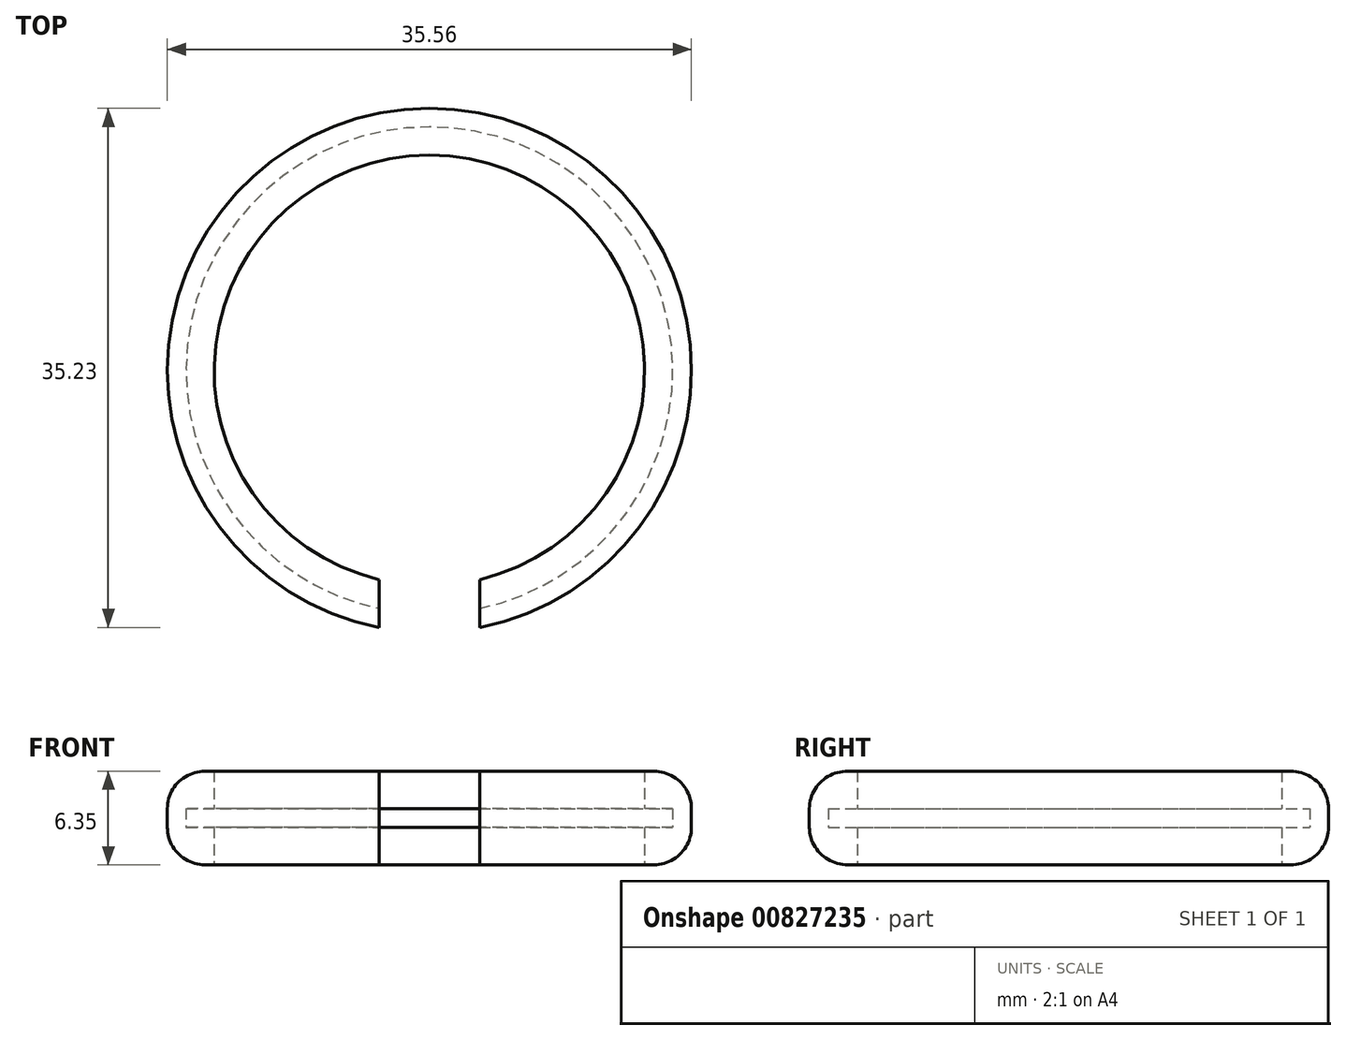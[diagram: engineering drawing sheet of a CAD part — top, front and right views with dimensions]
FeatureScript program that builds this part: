
annotation { "Feature Type Name" : "Feature", "Feature Type Description" : "" }
export const myFeature = defineFeature(function(context is Context, id is Id, definition is map)
    precondition{}
    {
        {
            var Q0;
            Q0=qCreatedBy(makeId("Top.planeOp"),FACE);
            var sketch = newSketch(context, id + "F0", { "sketchPlane" : qUnion([Q0])});
            skCircle(sketch, "E0", {"center": v(0, 0) * mm, "radius": 17.78 * mm});
            skSolve(sketch);
        }
        {
            var Q0;
            Q0=makeQuery(id+"F0.imprint","IMPRINT",FACE,{"disambiguationData":[TD([[makeQuery(id+"F0.imprint","IMPRINT",EDGE,{"derivedFrom":sQuery(id+"F0.wireOp",EDGE,"E0")}),1.0]])]});
            extrude(context, id + "F1", {"entities" : qUnion([Q0]), "depth" : 2.54 * mm, "offsetDistance" : 25.4 * mm});
        }
        {
            var Q0;
            Q0=makeQuery(id+"F1.opExtrude","CAP_FACE",FACE,{"disambiguationData":[OSD([sQuery(id+"F0.wireOp",EDGE,"E0")])],"isStart":false});
            var sketch = newSketch(context, id + "F2", { "sketchPlane" : qUnion([Q0])});
            skCircle(sketch, "E1", {"center": v(0, 0) * mm, "radius": 17.78 * mm});
            skCircle(sketch, "E2", {"center": v(0, 0) * mm, "radius": 16.51 * mm});
            skSolve(sketch);
        }
        {
            var Q0;
            Q0=makeQuery(id+"F2.imprint","IMPRINT",FACE,{"disambiguationData":[TD([[makeQuery(id+"F2.imprint","IMPRINT",EDGE,{"derivedFrom":sQuery(id+"F2.wireOp",EDGE,"E2")}),-1.0]])]});
            extrude(context, id + "F3", {"entities" : qUnion([Q0]), "operationType" : NewBodyOperationType.ADD, "depth" : 1.27 * mm, "offsetDistance" : 25.4 * mm});
        }
        {
            var Q0;
            Q0=makeQuery(id+"F3.opExtrude","CAP_FACE",FACE,{"disambiguationData":[OSD([sQuery(id+"F0.wireOp",EDGE,"E0"),sQuery(id+"F2.wireOp",EDGE,"E2")])],"isStart":false});
            var sketch = newSketch(context, id + "F4", { "sketchPlane" : qUnion([Q0])});
            skCircle(sketch, "E3", {"center": v(0, 0) * mm, "radius": 17.78 * mm});
            skSolve(sketch);
        }
        {
            var Q0;
            Q0=qSketchRegion(id+"F4",true);
            extrude(context, id + "F5", {"entities" : qUnion([Q0]), "operationType" : NewBodyOperationType.ADD, "depth" : 2.54 * mm, "offsetDistance" : 25.4 * mm});
        }
        {
            var Q0;
            Q0=makeQuery(id+"F1.opExtrude","CAP_FACE",FACE,{"disambiguationData":[OSD([sQuery(id+"F0.wireOp",EDGE,"E0")])],"isStart":true});
            var sketch = newSketch(context, id + "F6", { "sketchPlane" : qUnion([Q0])});
            skCircle(sketch, "E4", {"center": v(0, 0) * mm, "radius": 14.6 * mm});
            skSolve(sketch);
        }
        {
            var Q0;
            Q0=makeQuery(id+"F6.imprint","IMPRINT",FACE,{"disambiguationData":[TD([[makeQuery(id+"F6.imprint","IMPRINT",EDGE,{"derivedFrom":sQuery(id+"F6.wireOp",EDGE,"E4")}),1.0]])]});
            extrude(context, id + "F7", {"entities" : qUnion([Q0]), "operationType" : NewBodyOperationType.REMOVE, "oppositeDirection" : true, "depth" : 50.8 * mm, "offsetDistance" : 25.4 * mm});
        }
        {
            var Q0;
            Q0=makeQuery(id+"F5.opExtrude","CAP_EDGE",EDGE,{"disambiguationData":[OSD([sQuery(id+"F4.wireOp",EDGE,"E3")])],"isStart":false});
            var Q1;
            Q1=makeQuery(id+"F1.opExtrude","CAP_EDGE",EDGE,{"disambiguationData":[OSD([sQuery(id+"F0.wireOp",EDGE,"E0")])],"isStart":true});
            fillet(context, id + "F8", {"entities" : qUnion([Q0, Q1]), "radius" : 2.54 * mm, "tangentPropagation" : true, "allowEdgeOverflow" : false});
        }
        {
            var Q0;
            Q0=makeQuery(id+"F5.opExtrude","CAP_FACE",FACE,{"disambiguationData":[OSD([sQuery(id+"F4.wireOp",EDGE,"E3")])],"isStart":false});
            var sketch = newSketch(context, id + "F9", { "sketchPlane" : qUnion([Q0])});
            skLineSegment(sketch, "E5.bottom", {"start": v(3.4, -22.17) * mm, "end": v(-3.4, -22.17) * mm});
            skLineSegment(sketch, "E5.top", {"start": v(3.4, -10.82) * mm, "end": v(-3.4, -10.82) * mm});
            skLineSegment(sketch, "E5.left", {"start": v(3.4, -22.17) * mm, "end": v(3.4, -10.82) * mm});
            skLineSegment(sketch, "E5.right", {"start": v(-3.4, -22.17) * mm, "end": v(-3.4, -10.82) * mm});
            skPoint(sketch, "E5.middle", {"position": v(0, -16.5) * mm});
            skSolve(sketch);
        }
        {
            var Q0;
            {var subQ0=sQuery(id+"F9.wireOp",EDGE,"E5.bottom");Q0=makeQuery(id+"F9.imprint","IMPRINT",FACE,{"disambiguationData":[TD([[makeQuery(id+"F9.imprint","IMPRINT",EDGE,{"derivedFrom":subQ0}),-1.0]])]});}
            var Q1;
            {var subQ0=sQuery(id+"F9.wireOp",EDGE,"E5.top");Q1=makeQuery(id+"F9.imprint","IMPRINT",FACE,{"disambiguationData":[TD([[makeQuery(id+"F9.imprint","IMPRINT",EDGE,{"derivedFrom":subQ0}),1.0]])]});}
            var Q2;
            {var subQ0=sQuery(id+"F9.wireOp",EDGE,"E5.left");var subQ1=sQuery(id+"F4.wireOp",EDGE,"E3");var subQ2=makeQuery(id+"F5.opExtrude","CAP_FACE",FACE,{"disambiguationData":[OSD([subQ1])],"isStart":false});var subQ3=makeQuery(id+"F8.opFillet","BLEND_EDGE",EDGE,{"blendedFrom":[makeQuery(id+"F5.opExtrude","CAP_EDGE",EDGE,{"disambiguationData":[OSD([subQ1])],"isStart":false}),subQ2],"blendedInto":[subQ2]});var subQ4=makeQuery(id+"F9.imprint","INTERSECT",VERTEX,{"derivedFrom":[subQ3,subQ0]});Q2=makeQuery(id+"F9.imprint","IMPRINT",FACE,{"disambiguationData":[TD([[makeQuery(id+"F9.imprint","IMPRINT",EDGE,{"disambiguationData":[TD([[subQ4,-1.0]])],"derivedFrom":subQ0}),1.0]])]});}
            extrude(context, id + "F10", {"entities" : qUnion([Q0, Q1, Q2]), "operationType" : NewBodyOperationType.REMOVE, "oppositeDirection" : true, "depth" : 30.73 * mm, "offsetDistance" : 25.4 * mm});
        }
    });
